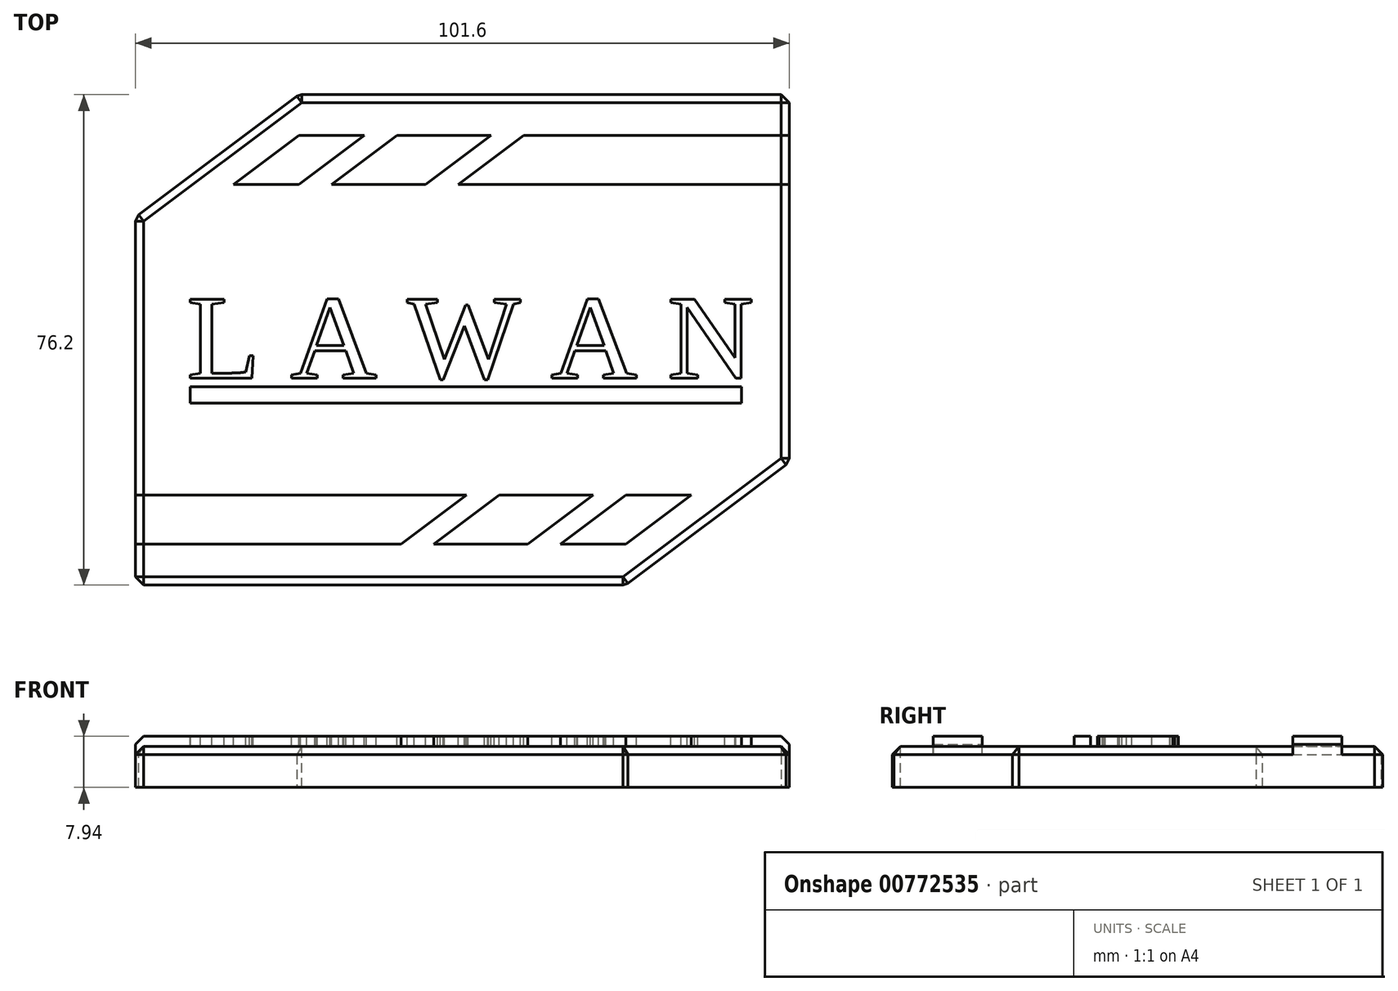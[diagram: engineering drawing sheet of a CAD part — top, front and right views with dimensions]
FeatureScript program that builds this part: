
annotation { "Feature Type Name" : "Feature", "Feature Type Description" : "" }
export const myFeature = defineFeature(function(context is Context, id is Id, definition is map)
    precondition{}
    {
        {
            var Q0;
            Q0=qCreatedBy(makeId("Top.planeOp"),FACE);
            var sketch = newSketch(context, id + "F0", { "sketchPlane" : qUnion([Q0])});
            skLineSegment(sketch, "E0.bottom", {"start": v(-50.8, -38.1) * mm, "end": v(25.4, -38.1) * mm});
            skLineSegment(sketch, "E0.top", {"start": v(-25.4, 38.1) * mm, "end": v(50.8, 38.1) * mm});
            skLineSegment(sketch, "E0.left", {"start": v(-50.8, -38.1) * mm, "end": v(-50.8, 19.05) * mm});
            skLineSegment(sketch, "E0.right", {"start": v(50.8, -19.05) * mm, "end": v(50.8, 38.1) * mm});
            skLineSegment(sketch, "E1", {"start": v(-50.8, 19.05) * mm, "end": v(-25.4, 38.1) * mm});
            skLineSegment(sketch, "E2", {"start": v(25.4, -38.1) * mm, "end": v(50.8, -19.05) * mm});
            skPoint(sketch, "E3.orphan", {"position": v(-50.8, 38.1) * mm});
            skPoint(sketch, "E4.orphan", {"position": v(50.8, -38.1) * mm});
            skSolve(sketch);
        }
        {
            var Q0;
            Q0=makeQuery(id+"F0.imprint","IMPRINT",FACE,{"disambiguationData":[TD([[makeQuery(id+"F0.imprint","IMPRINT",EDGE,{"derivedFrom":sQuery(id+"F0.wireOp",EDGE,"E0.bottom")}),1.0]])]});
            extrude(context, id + "F1", {"entities" : qUnion([Q0]), "depth" : 6.35 * mm, "offsetDistance" : 25.4 * mm});
        }
        {
            var Q0;
            Q0=makeQuery(id+"F1.opExtrude","CAP_FACE",FACE,{"disambiguationData":[OSD([sQuery(id+"F0.wireOp",EDGE,"E0.bottom"),sQuery(id+"F0.wireOp",EDGE,"E0.top"),sQuery(id+"F0.wireOp",EDGE,"E0.left"),sQuery(id+"F0.wireOp",EDGE,"E0.right"),sQuery(id+"F0.wireOp",EDGE,"E1"),sQuery(id+"F0.wireOp",EDGE,"E2")])],"isStart":false});
            var sketch = newSketch(context, id + "F2", { "sketchPlane" : qUnion([Q0])});
            skText(sketch, "E5", { "text": "L A W A N", "fontName": "Tinos-Regular.ttf"});
            const initialGuessF2  = {"E5": [-0.0428, -0.00595, 1, 0, 0.01344]};
            skSetInitialGuess(sketch, initialGuessF2);
            skSolve(sketch);
        }
        {
            var Q0;
            Q0 = qSketchRegion(id + "F2", true);
            extrude(context, id + "F3", {"entities" : qUnion([Q0]), "operationType" : NewBodyOperationType.ADD, "endBound" : BoundingType.SYMMETRIC, "oppositeDirection" : true, "depth" : 3.17 * mm, "offsetDistance" : 25.4 * mm});
        }
        {
            var Q0;
            {var subQ0=sQuery(id+"F0.wireOp",EDGE,"E0.left");var subQ1=sQuery(id+"F0.wireOp",EDGE,"E2");var subQ2=sQuery(id+"F0.wireOp",EDGE,"E1");var subQ3=sQuery(id+"F0.wireOp",EDGE,"E0.bottom");var subQ4=sQuery(id+"F0.wireOp",EDGE,"E0.right");var subQ5=sQuery(id+"F0.wireOp",EDGE,"E0.top");Q0=makeQuery(id+"F3.boolean.opBoolean","SPLIT",FACE,{"disambiguationData":[TD([makeQuery(id+"F1.opExtrude","SWEPT_FACE",FACE,{"disambiguationData":[OSD([subQ3])]})])],"derivedFrom":makeQuery(id+"F1.opExtrude","CAP_FACE",FACE,{"disambiguationData":[OSD([subQ3,subQ5,subQ0,subQ4,subQ2,subQ1])],"isStart":false})});}
            var sketch = newSketch(context, id + "F4", { "sketchPlane" : qUnion([Q0])});
            skLineSegment(sketch, "E6", {"start": v(50.8, 31.75) * mm, "end": v(9.52, 31.75) * mm});
            skLineSegment(sketch, "E7", {"start": v(-25.4, 31.75) * mm, "end": v(-35.56, 24.13) * mm});
            skLineSegment(sketch, "E8", {"start": v(-35.56, 24.13) * mm, "end": v(-25.4, 24.13) * mm});
            skLineSegment(sketch, "E9", {"start": v(-25.4, 24.13) * mm, "end": v(-15.24, 31.75) * mm});
            skLineSegment(sketch, "E10", {"start": v(-20.32, 24.13) * mm, "end": v(-10.16, 31.75) * mm});
            skLineSegment(sketch, "E11.trimOffspring", {"start": v(-20.32, 24.13) * mm, "end": v(-5.72, 24.13) * mm});
            skLineSegment(sketch, "E12.trimOffspring", {"start": v(-15.24, 31.75) * mm, "end": v(-25.4, 31.75) * mm});
            skLineSegment(sketch, "E13", {"start": v(4.44, 31.75) * mm, "end": v(-5.72, 24.13) * mm});
            skLineSegment(sketch, "E14", {"start": v(-0.64, 24.13) * mm, "end": v(9.52, 31.75) * mm});
            skLineSegment(sketch, "E15.trimOffspring", {"start": v(-0.64, 24.13) * mm, "end": v(50.8, 24.13) * mm});
            skLineSegment(sketch, "E16.trimOffspring", {"start": v(4.44, 31.75) * mm, "end": v(-10.16, 31.75) * mm});
            skLineSegment(sketch, "E17.MirrorCS", {"start": v(-0.64, -24.13) * mm, "end": v(0.64, -24.13) * mm});
            skLineSegment(sketch, "E18.MirrorCS", {"start": v(25.4, -31.75) * mm, "end": v(15.24, -31.75) * mm});
            skLineSegment(sketch, "E19.MirrorCS", {"start": v(-0.64, -24.13) * mm, "end": v(0, -24.6) * mm});
            skLineSegment(sketch, "E20.MirrorCS", {"start": v(-20.32, -24.13) * mm, "end": v(-5.72, -24.13) * mm});
            skLineSegment(sketch, "E21.MirrorCS", {"start": v(4.44, -31.75) * mm, "end": v(-4.44, -31.75) * mm});
            skLineSegment(sketch, "E22.MirrorCS", {"start": v(-15.24, -31.75) * mm, "end": v(-25.4, -31.75) * mm});
            skLineSegment(sketch, "E23.MirrorCS", {"start": v(-35.56, -24.13) * mm, "end": v(-25.4, -24.13) * mm});
            skLineSegment(sketch, "E24.MirrorCS", {"start": v(-50.8, -31.75) * mm, "end": v(-9.52, -31.75) * mm});
            skLineSegment(sketch, "E25.MirrorCS", {"start": v(0.64, -24.13) * mm, "end": v(-50.8, -24.13) * mm});
            skLineSegment(sketch, "E26.MirrorCS", {"start": v(0.64, -24.13) * mm, "end": v(-9.52, -31.75) * mm});
            skLineSegment(sketch, "E27.MirrorCS", {"start": v(-4.44, -31.75) * mm, "end": v(5.72, -24.13) * mm});
            skLineSegment(sketch, "E28.MirrorCS", {"start": v(20.32, -24.13) * mm, "end": v(5.72, -24.13) * mm});
            skLineSegment(sketch, "E29.MirrorCS", {"start": v(20.32, -24.13) * mm, "end": v(10.16, -31.75) * mm});
            skLineSegment(sketch, "E30.MirrorCS", {"start": v(-4.44, -31.75) * mm, "end": v(10.16, -31.75) * mm});
            skLineSegment(sketch, "E31.MirrorCS", {"start": v(35.56, -24.13) * mm, "end": v(25.4, -24.13) * mm});
            skLineSegment(sketch, "E32.MirrorCS", {"start": v(25.4, -31.75) * mm, "end": v(35.56, -24.13) * mm});
            skLineSegment(sketch, "E33.MirrorCS", {"start": v(25.4, -24.13) * mm, "end": v(15.24, -31.75) * mm});
            skLineSegment(sketch, "E34.MirrorCS", {"start": v(15.24, -31.75) * mm, "end": v(25.4, -31.75) * mm});
            skLineSegment(sketch, "E35.trimOffspring", {"start": v(-9.52, -31.75) * mm, "end": v(-10.16, -31.75) * mm});
            skLineSegment(sketch, "E36.trimOffspring", {"start": v(5.72, -24.13) * mm, "end": v(20.32, -24.13) * mm});
            skLineSegment(sketch, "E37.trimOffspring", {"start": v(10.16, -31.75) * mm, "end": v(9.52, -31.75) * mm});
            skLineSegment(sketch, "E38.trimOffspring", {"start": v(25.4, -24.13) * mm, "end": v(35.56, -24.13) * mm});
            skSolve(sketch);
        }
        {
            var Q0;
            Q0 = qSketchRegion(id + "F4", true);
            var Q1;
            {var subQ7=sQuery(id+"F4.wireOp",EDGE,"E19.MirrorCS");Q1=makeQuery(id+"F4.imprint","IMPRINT",FACE,{"disambiguationData":[TD([[makeQuery(id+"F4.imprint","IMPRINT",EDGE,{"derivedFrom":subQ7}),-1.0]])]});}
            var Q2;
            {var subQ0=sQuery(id+"F4.wireOp",EDGE,"E6");Q2=makeQuery(id+"F4.imprint","IMPRINT",FACE,{"disambiguationData":[TD([[makeQuery(id+"F4.imprint","IMPRINT",EDGE,{"derivedFrom":subQ0}),1.0]])]});}
            extrude(context, id + "F5", {"entities" : qUnion([Q0, Q1, Q2]), "operationType" : NewBodyOperationType.ADD, "endBound" : BoundingType.SYMMETRIC, "oppositeDirection" : true, "depth" : 3.17 * mm, "offsetDistance" : 25.4 * mm});
        }
        {
            var Q0;
            {var subQ0=sQuery(id+"F0.wireOp",EDGE,"E0.left");var subQ1=sQuery(id+"F0.wireOp",EDGE,"E2");var subQ2=sQuery(id+"F0.wireOp",EDGE,"E1");var subQ3=sQuery(id+"F0.wireOp",EDGE,"E0.bottom");var subQ4=sQuery(id+"F0.wireOp",EDGE,"E0.right");var subQ5=sQuery(id+"F0.wireOp",EDGE,"E0.top");Q0=makeQuery(id+"F3.boolean.opBoolean","SPLIT",FACE,{"disambiguationData":[TD([makeQuery(id+"F1.opExtrude","SWEPT_FACE",FACE,{"disambiguationData":[OSD([subQ3])]})])],"derivedFrom":makeQuery(id+"F1.opExtrude","CAP_FACE",FACE,{"disambiguationData":[OSD([subQ3,subQ5,subQ0,subQ4,subQ2,subQ1])],"isStart":false})});}
            var sketch = newSketch(context, id + "F6", { "sketchPlane" : qUnion([Q0])});
            skLineSegment(sketch, "E39.bottom", {"start": v(-42.26, -7.28) * mm, "end": v(43.36, -7.28) * mm});
            skLineSegment(sketch, "E39.top", {"start": v(-42.26, -9.82) * mm, "end": v(43.36, -9.82) * mm});
            skLineSegment(sketch, "E39.left", {"start": v(-42.26, -7.28) * mm, "end": v(-42.26, -9.82) * mm});
            skLineSegment(sketch, "E39.right", {"start": v(43.36, -7.28) * mm, "end": v(43.36, -9.82) * mm});
            skSolve(sketch);
        }
        {
            var Q0;
            Q0=makeQuery(id+"F6.imprint","IMPRINT",FACE,{"disambiguationData":[TD([[makeQuery(id+"F6.imprint","IMPRINT",EDGE,{"derivedFrom":sQuery(id+"F6.wireOp",EDGE,"E39.bottom")}),-1.0]])]});
            extrude(context, id + "F7", {"entities" : qUnion([Q0]), "operationType" : NewBodyOperationType.ADD, "endBound" : BoundingType.SYMMETRIC, "depth" : 3.17 * mm, "offsetDistance" : 25.4 * mm});
        }
        {
            var Q0;
            Q0=makeQuery(id+"F1.opExtrude","CAP_EDGE",EDGE,{"disambiguationData":[OSD([sQuery(id+"F0.wireOp",EDGE,"E0.bottom")])],"isStart":false});
            var Q1;
            Q1=makeQuery(id+"F1.opExtrude","CAP_EDGE",EDGE,{"disambiguationData":[OSD([sQuery(id+"F0.wireOp",EDGE,"E2")])],"isStart":false});
            var Q2;
            {var subQ0=sQuery(id+"F0.wireOp",EDGE,"E0.right");var subQ1=sQuery(id+"F0.wireOp",EDGE,"E2");Q2=makeQuery(id+"F5.boolean.opBoolean","SPLIT",EDGE,{"disambiguationData":[TD([makeQuery(id+"F1.opExtrude","SWEPT_FACE",FACE,{"disambiguationData":[OSD([subQ1])]})])],"derivedFrom":makeQuery(id+"F1.opExtrude","CAP_EDGE",EDGE,{"disambiguationData":[OSD([subQ0])],"isStart":false})});}
            var Q3;
            Q3=makeQuery(id+"F5.opExtrude","CAP_EDGE",EDGE,{"disambiguationData":[OSD([sQuery(id+"F0.wireOp",EDGE,"E0.right")])],"isStart":true});
            var Q4;
            {var subQ0=sQuery(id+"F0.wireOp",EDGE,"E0.right");var subQ1=sQuery(id+"F0.wireOp",EDGE,"E0.top");Q4=makeQuery(id+"F5.boolean.opBoolean","SPLIT",EDGE,{"disambiguationData":[TD([makeQuery(id+"F1.opExtrude","SWEPT_FACE",FACE,{"disambiguationData":[OSD([subQ1])]})])],"derivedFrom":makeQuery(id+"F1.opExtrude","CAP_EDGE",EDGE,{"disambiguationData":[OSD([subQ0])],"isStart":false})});}
            var Q5;
            Q5=makeQuery(id+"F1.opExtrude","CAP_EDGE",EDGE,{"disambiguationData":[OSD([sQuery(id+"F0.wireOp",EDGE,"E0.top")])],"isStart":false});
            var Q6;
            Q6=makeQuery(id+"F1.opExtrude","CAP_EDGE",EDGE,{"disambiguationData":[OSD([sQuery(id+"F0.wireOp",EDGE,"E1")])],"isStart":false});
            var Q7;
            {var subQ0=sQuery(id+"F0.wireOp",EDGE,"E1");var subQ1=sQuery(id+"F0.wireOp",EDGE,"E0.left");Q7=makeQuery(id+"F5.boolean.opBoolean","SPLIT",EDGE,{"disambiguationData":[TD([makeQuery(id+"F1.opExtrude","SWEPT_FACE",FACE,{"disambiguationData":[OSD([subQ0])]})])],"derivedFrom":makeQuery(id+"F1.opExtrude","CAP_EDGE",EDGE,{"disambiguationData":[OSD([subQ1])],"isStart":false})});}
            var Q8;
            Q8=makeQuery(id+"F5.opExtrude","CAP_EDGE",EDGE,{"disambiguationData":[OSD([sQuery(id+"F0.wireOp",EDGE,"E0.left")])],"isStart":true});
            var Q9;
            {var subQ0=sQuery(id+"F0.wireOp",EDGE,"E0.left");var subQ1=sQuery(id+"F0.wireOp",EDGE,"E0.bottom");Q9=makeQuery(id+"F5.boolean.opBoolean","SPLIT",EDGE,{"disambiguationData":[TD([makeQuery(id+"F1.opExtrude","SWEPT_FACE",FACE,{"disambiguationData":[OSD([subQ1])]})])],"derivedFrom":makeQuery(id+"F1.opExtrude","CAP_EDGE",EDGE,{"disambiguationData":[OSD([subQ0])],"isStart":false})});}
            var Q10;
            Q10=makeQuery(id+"F1.opExtrude","SWEPT_EDGE",EDGE,{"disambiguationData":[OSD([sQuery(id+"F0.wireOp",EDGE,"E0.bottom"),sQuery(id+"F0.wireOp",EDGE,"E2")])]});
            var Q11;
            Q11=makeQuery(id+"F1.opExtrude","SWEPT_EDGE",EDGE,{"disambiguationData":[OSD([sQuery(id+"F0.wireOp",EDGE,"E0.right"),sQuery(id+"F0.wireOp",EDGE,"E2")])]});
            var Q12;
            Q12=makeQuery(id+"F1.opExtrude","SWEPT_EDGE",EDGE,{"disambiguationData":[OSD([sQuery(id+"F0.wireOp",EDGE,"E0.bottom"),sQuery(id+"F0.wireOp",EDGE,"E0.left")])]});
            var Q13;
            Q13=makeQuery(id+"F1.opExtrude","SWEPT_EDGE",EDGE,{"disambiguationData":[OSD([sQuery(id+"F0.wireOp",EDGE,"E0.left"),sQuery(id+"F0.wireOp",EDGE,"E1")])]});
            var Q14;
            Q14=makeQuery(id+"F1.opExtrude","SWEPT_EDGE",EDGE,{"disambiguationData":[OSD([sQuery(id+"F0.wireOp",EDGE,"E0.top"),sQuery(id+"F0.wireOp",EDGE,"E1")])]});
            var Q15;
            Q15=makeQuery(id+"F1.opExtrude","SWEPT_EDGE",EDGE,{"disambiguationData":[OSD([sQuery(id+"F0.wireOp",EDGE,"E0.top"),sQuery(id+"F0.wireOp",EDGE,"E0.right")])]});
            chamfer(context, id + "F8", {"entities" : qUnion([Q0, Q1, Q2, Q3, Q4, Q5, Q6, Q7, Q8, Q9, Q10, Q11, Q12, Q13, Q14, Q15]), "width" : 1.27 * mm, "tangentPropagation" : true});
        }
    });
